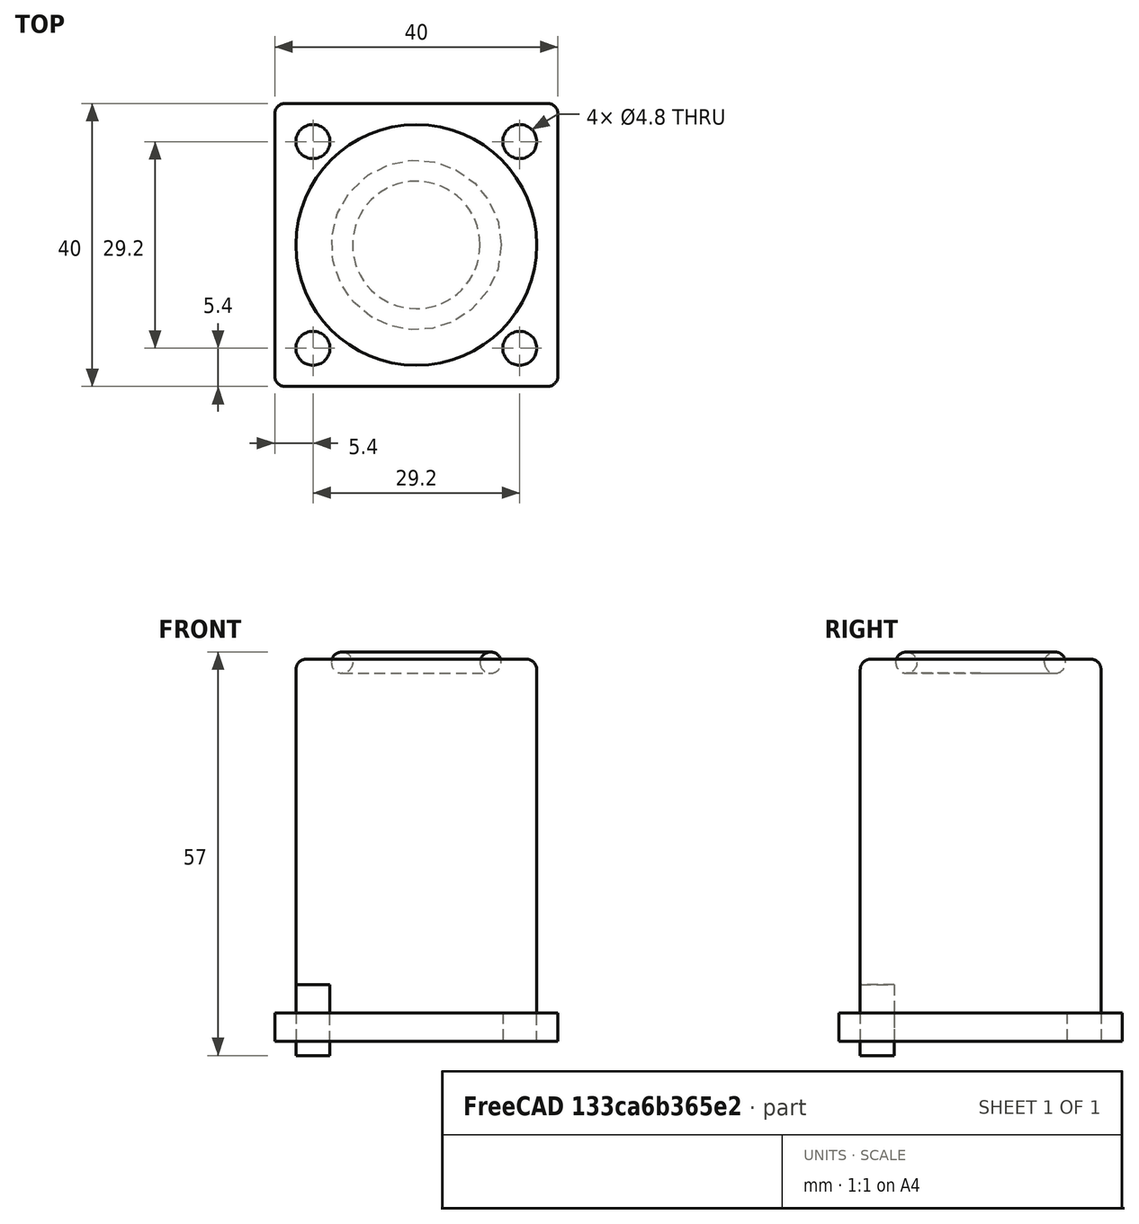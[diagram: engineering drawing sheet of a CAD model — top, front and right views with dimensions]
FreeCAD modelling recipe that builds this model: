
FCSTD DOCUMENT  (FreeCAD 0.21R33771 (Git))
Label: OJT1_T15R03_pota_taula
License: All rights reserved
LicenseURL: http://en.wikipedia.org/wiki/All_rights_reserved
objects: Part::Cylinder×2, Part::Fillet×2, Part::Box×1, Part::FeaturePython×1, Part::Torus×1, Part::Cut×1, Part::Fuse×1
note: 8 computed .brp shape members not serialized (recipe doc carries the construction recipe); baked Part::Feature solids carry a one-line shape summary decoded from their .brp

FEATURE [Part::Box] Box  label="Cube"
  AttacherType = Attacher::AttachEngine3D
  Height = 4
  Length = 40
  Width = 40
FEATURE [Part::Cylinder] Cylinder
  Angle = 360
  AttacherType = Attacher::AttachEngine3D
  FirstAngle = 0
  Height = 10
  Placement = pos=(5.4,5.4,-2) rot=(0,0,1;0rad)
  Radius = 2.4
  SecondAngle = 0
FEATURE [Part::FeaturePython] Array  # Draft array (typed FeaturePython)
  AlwaysSyncPlacement = false
  Angle = 360
  ArrayType = 0
  Axis = (0,0,1)
  Base = -> Cylinder
  Center = (0,0,0)
  Count = 4
  ExpandArray = false
  Fuse = false
  IntervalAxis = (0,0,0)
  IntervalX = (29.2,0,0)
  IntervalY = (0,29.2,0)
  IntervalZ = (0,0,100)
  NumberCircles = 3
  NumberPolar = 5
  NumberX = 2
  NumberY = 2
  NumberZ = 1
  PlacementList = 4 placements: [(5.4,5.4,-2),(5.4,34.6,-2),(34.6,5.4,-2),(34.6,34.6,-2)]
  RadialDistance = 50
  ScaleList = (4) [(1,1,1),(1,1,1),(1,1,1),(1,1,1)]
  Symmetry = 1
  TangentialDistance = 25
FEATURE [Part::Cylinder] Cylinder001  label="pota"
  Angle = 360
  AttacherType = Attacher::AttachEngine3D
  FirstAngle = 0
  Height = 50
  Placement = pos=(20,20,4) rot=(0,0,1;0rad)
  Radius = 17
  SecondAngle = 0
FEATURE [Part::Torus] Torus
  Angle1 = -180
  Angle2 = 180
  Angle3 = 360
  AttacherType = Attacher::AttachEngine3D
  Placement = pos=(20,20,53.5) rot=(0,0,1;0rad)
  Radius1 = 10.5
  Radius2 = 1.5
FEATURE [Part::Cut] Cut
  Base = -> Box
  Refine = true
  Tool = -> Array
FEATURE [Part::Fillet] Fillet  label="base"
  Base = -> Cut
  Edges = 4 edges r=1.5: [Edge1,Edge3,Edge6,Edge15]
FEATURE [Part::Fillet] Fillet001  label="pota001"
  Base = -> Cylinder001
  Edges = 1 edges r=1.5: [Edge3]
FEATURE [Part::Fuse] Fusion
  Base = -> Fillet
  Refine = true
  Tool = -> Fillet001
